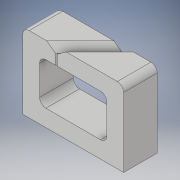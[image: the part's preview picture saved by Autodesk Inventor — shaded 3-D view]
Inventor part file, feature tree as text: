
AUTODESK INVENTOR PART (.ipt)
format: ipt  version: 2019 (Build 230136000, 136)  size: 143,360 bytes
history: native  units: mm
features: extrude x2, sketch x2, chamfer x1, fillet x1
ambient origin geometry x8: Origin, YZ Plane, XZ Plane, XY Plane, X Axis, Y Axis, Z Axis, Center Point
bodies: Solid1 (feature_tree)
feature tree (6):
  extrude  "Extrusion1"  Depth=2.0mm
  extrude  "Extrusion2"  Depth=0.75mm
  chamfer  "Chamfer1"  Distance=2.0mm
  fillet  "Fillet1"  Radius=1.25mm
  sketch  "Sketch1"  dims[d0=2.0mm d1=2.5mm]
  sketch  "Sketch2"  dims[d2=2.5mm d3=1.25mm d4=2.0mm d5=1.25mm d6=1.0mm d7=5.0mm d8=8.0mm d9=2.0mm d10=4.0mm d11=0.0mm d12=2.0mm d13=2.0mm d15=0.1mm d16=0.1mm d17=4.0mm d18=0.0mm d19=0.75mm d20=2.0mm d21=45.0deg d22=0.75mm d23=0.75mm]
